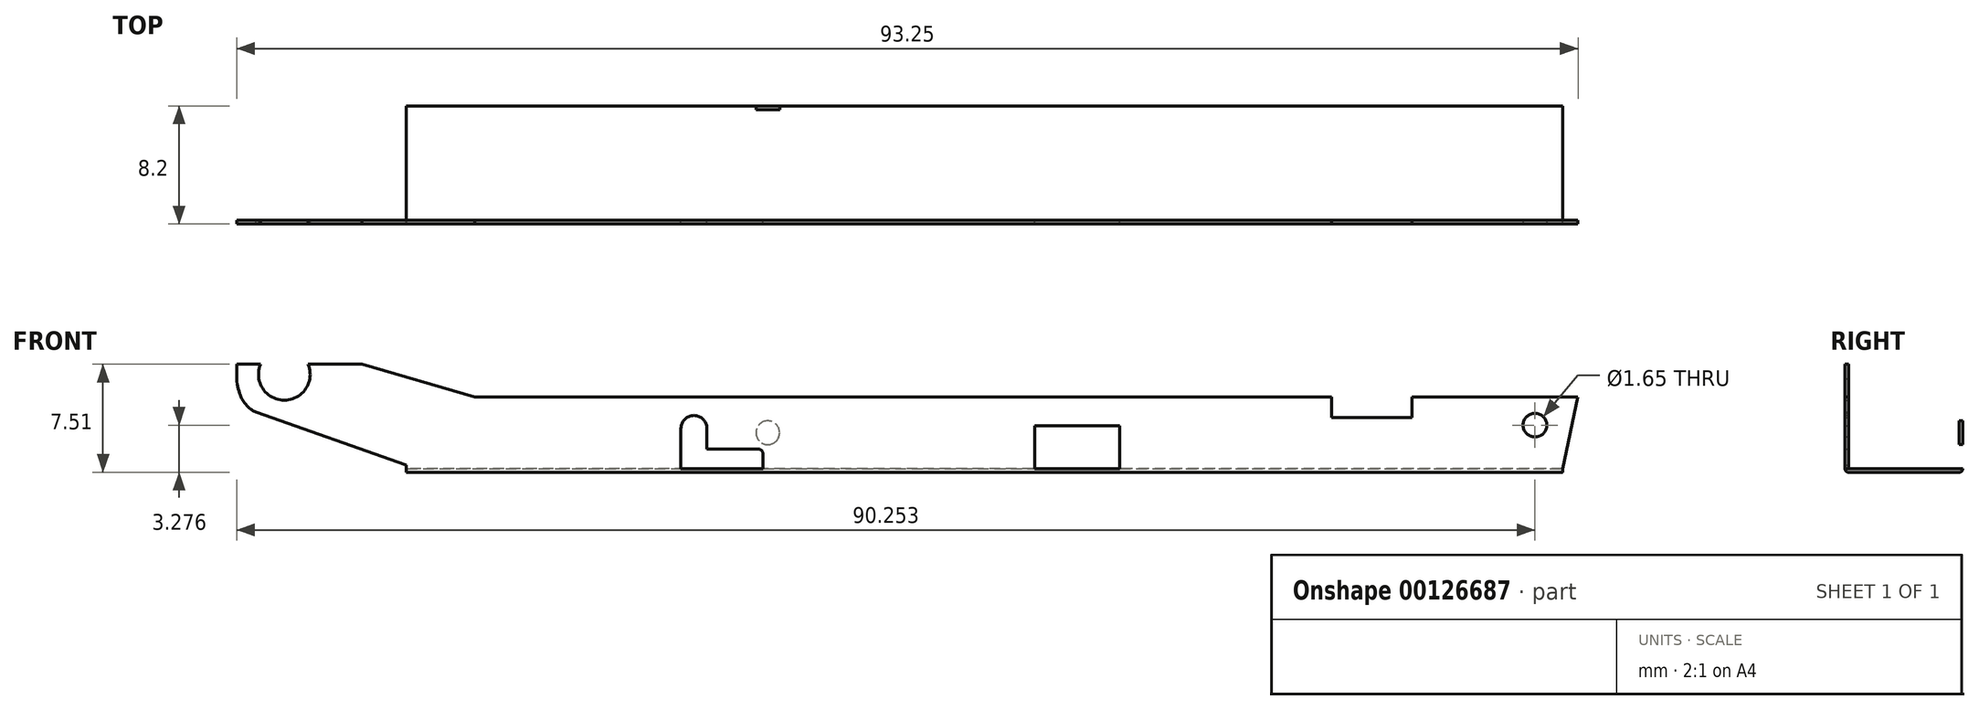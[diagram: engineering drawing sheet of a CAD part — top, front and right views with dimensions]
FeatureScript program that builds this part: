
annotation { "Feature Type Name" : "Feature", "Feature Type Description" : "" }
export const myFeature = defineFeature(function(context is Context, id is Id, definition is map)
    precondition{}
    {
        {
            var Q0;
            Q0=qCreatedBy(makeId("Front.planeOp"),FACE);
            var sketch = newSketch(context, id + "F0", { "sketchPlane" : qUnion([Q0])});
            skLineSegment(sketch, "E0", {"start": v(-40.19, 0) * mm, "end": v(40.19, 0) * mm});
            skLineSegment(sketch, "E1", {"start": v(-40.19, 0) * mm, "end": v(-40.19, 0.25) * mm});
            skLineSegment(sketch, "E2", {"start": v(-40.19, 0) * mm, "end": v(-51.99, 0) * mm, "construction": true});
            skLineSegment(sketch, "E3", {"start": v(-51.99, 0) * mm, "end": v(-51.99, 7.26) * mm});
            skLineSegment(sketch, "E4", {"start": v(-51.99, 7.26) * mm, "end": v(-50.33, 7.26) * mm});
            skPoint(sketch, "E5", {"position": v(-50.33, 7.26) * mm});
            skPoint(sketch, "E6", {"position": v(-47.03, 7.26) * mm});
            skArc(sketch, "E7", {"start": v(-50.33, 7.26) * mm, "mid": v(-48.67, 4.76) * mm, "end": v(-47.03, 7.26) * mm});
            skPoint(sketch, "E8", {"position": v(-48.68, 4.76) * mm});
            skLineSegment(sketch, "E9", {"start": v(-43.27, 7.26) * mm, "end": v(-43.27, 5) * mm, "construction": true});
            skLineSegment(sketch, "E10", {"start": v(-43.27, 5) * mm, "end": v(-35.45, 5) * mm, "construction": true});
            skLineSegment(sketch, "E11", {"start": v(-43.27, 7.26) * mm, "end": v(-35.45, 5) * mm});
            skLineSegment(sketch, "E12", {"start": v(-35.45, 5) * mm, "end": v(24.12, 5) * mm});
            skLineSegment(sketch, "E13", {"start": v(41.26, 5) * mm, "end": v(40.19, 0) * mm});
            skLineSegment(sketch, "E14", {"start": v(-40.18, 0.25) * mm, "end": v(-50.66, 3.94) * mm});
            skFitSpline(sketch, "E15", {"points": [v(-51.99, 7.26) * mm, v(-50.66, 3.94) * mm], "startDerivative": vector(-0.48, -6.82) * mm, "endDerivative": vector(1.78, -0.73) * mm});
            skLineSegment(sketch, "E16", {"start": v(-52.15, 4.99) * mm, "end": v(-51.99, 4.99) * mm});
            skLineSegment(sketch, "E17", {"start": v(-51.25, 4.18) * mm, "end": v(-51.99, 4.18) * mm});
            skLineSegment(sketch, "E18", {"start": v(-51.25, 4.18) * mm, "end": v(-50.66, 3.94) * mm});
            skPoint(sketch, "E19", {"position": v(29.7, 5) * mm});
            skPoint(sketch, "E20", {"position": v(24.12, 5) * mm});
            skLineSegment(sketch, "E21", {"start": v(29.7, 5) * mm, "end": v(29.7, 3.55) * mm});
            skLineSegment(sketch, "E22", {"start": v(24.12, 5) * mm, "end": v(24.12, 3.55) * mm});
            skLineSegment(sketch, "E23", {"start": v(24.12, 3.55) * mm, "end": v(29.7, 3.55) * mm});
            skLineSegment(sketch, "E24.trimOffspring", {"start": v(29.7, 5) * mm, "end": v(41.26, 5) * mm});
            skLineSegment(sketch, "E25.trimOffspring", {"start": v(-47.03, 7.26) * mm, "end": v(-43.27, 7.26) * mm});
            skLineSegment(sketch, "E26", {"start": v(-40.19, 0) * mm, "end": v(3.5, 0) * mm});
            skPoint(sketch, "E27", {"position": v(9.4, 0) * mm});
            skLineSegment(sketch, "E28", {"start": v(3.5, 0) * mm, "end": v(3.5, 2.98) * mm});
            skLineSegment(sketch, "E29", {"start": v(3.5, 2.98) * mm, "end": v(9.4, 2.98) * mm});
            skLineSegment(sketch, "E30", {"start": v(9.4, 2.98) * mm, "end": v(9.4, 0) * mm});
            skPoint(sketch, "E31", {"position": v(-21.1, 0) * mm});
            skPoint(sketch, "E32", {"position": v(-15.4, 0) * mm});
            skLineSegment(sketch, "E33", {"start": v(-21.1, 0) * mm, "end": v(-21.1, 2.8) * mm});
            skLineSegment(sketch, "E34", {"start": v(-15.4, 0) * mm, "end": v(-15.4, 1.04) * mm});
            skLineSegment(sketch, "E35", {"start": v(-15.73, 1.37) * mm, "end": v(-19.3, 1.37) * mm});
            skLineSegment(sketch, "E36", {"start": v(-19.3, 1.37) * mm, "end": v(-19.3, 2.8) * mm});
            skArc(sketch, "E37", {"start": v(-19.3, 2.8) * mm, "mid": v(-20.2, 3.7) * mm, "end": v(-21.1, 2.8) * mm});
            skPoint(sketch, "E38.visualSharp", {"position": v(-15.4, 1.37) * mm});
            skArc(sketch, "E38.filletArc", {"start": v(-15.4, 1.04) * mm, "mid": v(-15.5, 1.27) * mm, "end": v(-15.73, 1.37) * mm});
            skSolve(sketch);
        }
        {
            var Q0;
            Q0=qCreatedBy(makeId("Front.planeOp"),FACE);
            cPlane(context, id + "F1", {"entities" : qUnion([Q0]), "cplaneType" : CPlaneType.OFFSET, "offset" : 7.7 * mm, "oppositeDirection" : true, "width" : 150 * mm, "height" : 150 * mm});
        }
        {
            var Q0;
            Q0=qCreatedBy(id+"F1.planeOp",FACE);
            var sketch = newSketch(context, id + "F2", { "sketchPlane" : qUnion([Q0])});
            skLineSegment(sketch, "E39.0.0", {"start": v(9.4, 2.98) * mm, "end": v(9.4, 0) * mm});
            skLineSegment(sketch, "E39.0.1", {"start": v(9.4, 0) * mm, "end": v(40.19, 0) * mm});
            skLineSegment(sketch, "E39.0.2", {"start": v(40.19, 0) * mm, "end": v(41.26, 5) * mm});
            skLineSegment(sketch, "E39.0.3", {"start": v(41.26, 5) * mm, "end": v(29.7, 5) * mm});
            skLineSegment(sketch, "E39.0.4", {"start": v(29.7, 5) * mm, "end": v(29.7, 3.55) * mm});
            skLineSegment(sketch, "E39.0.5", {"start": v(29.7, 3.55) * mm, "end": v(24.12, 3.55) * mm});
            skLineSegment(sketch, "E39.0.6", {"start": v(24.12, 3.55) * mm, "end": v(24.12, 5) * mm});
            skLineSegment(sketch, "E39.0.7", {"start": v(24.12, 5) * mm, "end": v(-35.45, 5) * mm});
            skLineSegment(sketch, "E39.0.8", {"start": v(-35.45, 5) * mm, "end": v(-43.27, 7.26) * mm});
            skLineSegment(sketch, "E39.0.9", {"start": v(-43.27, 7.26) * mm, "end": v(-47.03, 7.26) * mm});
            skArc(sketch, "E39.0.10", {"start": v(-47.03, 7.26) * mm, "mid": v(-48.68, 4.76) * mm, "end": v(-50.33, 7.26) * mm});
            skLineSegment(sketch, "E39.0.11", {"start": v(-50.33, 7.26) * mm, "end": v(-51.99, 7.26) * mm});
            skLineSegment(sketch, "E39.0.12", {"start": v(-51.99, 7.26) * mm, "end": v(-51.99, 6.26) * mm});
            skFitSpline(sketch, "E39.0.13", {"points": [v(-51.99, 7.26) * mm, v(-52.15, 4.99) * mm, v(-51.25, 4.18) * mm, v(-50.66, 3.94) * mm]});
            skLineSegment(sketch, "E39.0.14", {"start": v(-50.66, 3.94) * mm, "end": v(-40.18, 0.25) * mm});
            skLineSegment(sketch, "E39.0.15", {"start": v(-40.19, 0.25) * mm, "end": v(-40.19, 0) * mm});
            skLineSegment(sketch, "E39.0.16", {"start": v(-40.19, 0) * mm, "end": v(-21.1, 0) * mm});
            skLineSegment(sketch, "E39.0.23", {"start": v(-15.4, 0) * mm, "end": v(3.5, 0) * mm});
            skLineSegment(sketch, "E39.0.24", {"start": v(3.5, 0) * mm, "end": v(3.5, 2.98) * mm});
            skLineSegment(sketch, "E39.0.25", {"start": v(3.5, 2.98) * mm, "end": v(9.4, 2.98) * mm});
            skLineSegment(sketch, "E40.0", {"start": v(-40.19, 0) * mm, "end": v(3.5, 0) * mm});
            skLineSegment(sketch, "E41.0", {"start": v(-40.19, 0) * mm, "end": v(40.19, 0) * mm});
            skSolve(sketch);
        }
        {
            var Q0;
            {var subQ5=sQuery(id+"F0.wireOp",EDGE,"E1");Q0=makeQuery(id+"F0.imprint","IMPRINT",FACE,{"disambiguationData":[TD([[makeQuery(id+"F0.imprint","IMPRINT",EDGE,{"derivedFrom":subQ5}),-1.0]])]});}
            extrude(context, id + "F3", {"entities" : qUnion([Q0]), "depth" : 0.25 * mm});
        }
        {
            var Q0;
            {var subQ4=sQuery(id+"F2.wireOp",EDGE,"E39.0.0");Q0=makeQuery(id+"F2.imprint","IMPRINT",FACE,{"disambiguationData":[TD([[makeQuery(id+"F2.imprint","IMPRINT",EDGE,{"derivedFrom":subQ4}),1.0]])]});}
            extrude(context, id + "F4", {"entities" : qUnion([Q0]), "oppositeDirection" : true, "depth" : 0.25 * mm});
        }
        {
            var Q0;
            Q0=qCreatedBy(makeId("Top.planeOp"),FACE);
            var sketch = newSketch(context, id + "F5", { "sketchPlane" : qUnion([Q0])});
            skPoint(sketch, "E42.0", {"position": v(40.19, 0) * mm});
            skPoint(sketch, "E43.0", {"position": v(40.19, 7.7) * mm});
            skPoint(sketch, "E44.0", {"position": v(-40.19, 0) * mm});
            skPoint(sketch, "E45.0", {"position": v(-40.18, 7.7) * mm});
            skLineSegment(sketch, "E46.bottom", {"start": v(40.18, 0) * mm, "end": v(-40.18, 0) * mm});
            skLineSegment(sketch, "E46.top", {"start": v(40.18, 7.7) * mm, "end": v(-40.18, 7.7) * mm});
            skLineSegment(sketch, "E46.left", {"start": v(40.19, 0) * mm, "end": v(40.19, 7.7) * mm});
            skLineSegment(sketch, "E46.right", {"start": v(-40.18, 0) * mm, "end": v(-40.18, 7.7) * mm});
            skSolve(sketch);
        }
        {
            var Q0;
            Q0=makeQuery(id+"F5.imprint","IMPRINT",FACE,{"disambiguationData":[TD([[makeQuery(id+"F5.imprint","IMPRINT",EDGE,{"derivedFrom":sQuery(id+"F5.wireOp",EDGE,"E46.bottom")}),-1.0]])]});
            extrude(context, id + "F6", {"entities" : qUnion([Q0]), "oppositeDirection" : true, "depth" : 0.25 * mm});
        }
        {
            var Q0;
            Q0=makeQuery(id+"F6.opExtrude","SWEPT_FACE",FACE,{"disambiguationData":[OSD([sQuery(id+"F5.wireOp",EDGE,"E46.right")])]});
            var sketch = newSketch(context, id + "F7", { "sketchPlane" : qUnion([Q0])});
            skPoint(sketch, "E47.0", {"position": v(0.25, 0) * mm});
            skPoint(sketch, "E48.0", {"position": v(0, -0.25) * mm});
            skArc(sketch, "E49", {"start": v(0, -0.25) * mm, "mid": v(0.18, -0.18) * mm, "end": v(0.25, 0) * mm});
            skLineSegment(sketch, "E50", {"start": v(0.25, 0) * mm, "end": v(0, 0) * mm});
            skLineSegment(sketch, "E51", {"start": v(0, 0) * mm, "end": v(0, -0.25) * mm});
            skSolve(sketch);
        }
        {
            var Q0;
            Q0=makeQuery(id+"F7.imprint","IMPRINT",FACE,{"disambiguationData":[TD([[makeQuery(id+"F7.imprint","IMPRINT",EDGE,{"derivedFrom":sQuery(id+"F7.wireOp",EDGE,"E49")}),1.0]])]});
            var Q1;
            Q1 = qConstructionFilter(qBodyType(qCreatedBy(id + "F7" ,EDGE), BodyType.WIRE), ConstructionObject.NO);
            var Q2;
            Q2=makeQuery(id+"F6.opExtrude","SWEPT_FACE",FACE,{"disambiguationData":[OSD([sQuery(id+"F5.wireOp",EDGE,"E46.left")])]});
            extrude(context, id + "F8", {"entities" : qUnion([Q0]), "operationType" : NewBodyOperationType.ADD, "surfaceEntities" : qUnion([Q1]), "endBound" : BoundingType.UP_TO_SURFACE, "oppositeDirection" : true, "endBoundEntityFace" : qUnion([Q2]), "depth" : 1.77 * mm});
        }
        {
            var Q0;
            Q0=makeQuery(id+"F6.opExtrude","SWEPT_FACE",FACE,{"disambiguationData":[OSD([sQuery(id+"F5.wireOp",EDGE,"E46.right")])]});
            var sketch = newSketch(context, id + "F9", { "sketchPlane" : qUnion([Q0])});
            skPoint(sketch, "E52.0", {"position": v(-7.95, 0) * mm});
            skArc(sketch, "E53", {"start": v(-7.95, 0) * mm, "mid": v(-7.88, -0.18) * mm, "end": v(-7.7, -0.25) * mm});
            skLineSegment(sketch, "E54", {"start": v(-7.7, 0) * mm, "end": v(-7.95, 0) * mm});
            skLineSegment(sketch, "E55", {"start": v(-7.7, 0) * mm, "end": v(-7.7, -0.25) * mm});
            skSolve(sketch);
        }
        {
            var Q0;
            Q0=makeQuery(id+"F9.imprint","IMPRINT",FACE,{"disambiguationData":[TD([[makeQuery(id+"F9.imprint","IMPRINT",EDGE,{"derivedFrom":sQuery(id+"F9.wireOp",EDGE,"E53")}),1.0]])]});
            var Q1;
            Q1=makeQuery(id+"F6.opExtrude","SWEPT_FACE",FACE,{"disambiguationData":[OSD([sQuery(id+"F5.wireOp",EDGE,"E46.left")])]});
            extrude(context, id + "F10", {"entities" : qUnion([Q0]), "operationType" : NewBodyOperationType.ADD, "endBound" : BoundingType.UP_TO_SURFACE, "oppositeDirection" : true, "endBoundEntityFace" : qUnion([Q1]), "depth" : 25 * mm});
        }
        {
            var Q0;
            Q0=makeQuery(id+"F3.opExtrude","CAP_FACE",FACE,{"disambiguationData":[OSD([sQuery(id+"F0.wireOp",EDGE,"E0"),sQuery(id+"F0.wireOp",EDGE,"E1"),sQuery(id+"F0.wireOp",EDGE,"E3"),sQuery(id+"F0.wireOp",EDGE,"E4"),sQuery(id+"F0.wireOp",EDGE,"E7"),sQuery(id+"F0.wireOp",EDGE,"E11"),sQuery(id+"F0.wireOp",EDGE,"E12"),sQuery(id+"F0.wireOp",EDGE,"E13"),sQuery(id+"F0.wireOp",EDGE,"E14"),sQuery(id+"F0.wireOp",EDGE,"E15"),sQuery(id+"F0.wireOp",EDGE,"E21"),sQuery(id+"F0.wireOp",EDGE,"E22"),sQuery(id+"F0.wireOp",EDGE,"E23"),sQuery(id+"F0.wireOp",EDGE,"E24.trimOffspring"),sQuery(id+"F0.wireOp",EDGE,"E25.trimOffspring"),sQuery(id+"F0.wireOp",EDGE,"E26"),sQuery(id+"F0.wireOp",EDGE,"E28"),sQuery(id+"F0.wireOp",EDGE,"E29"),sQuery(id+"F0.wireOp",EDGE,"E30"),sQuery(id+"F0.wireOp",EDGE,"E33"),sQuery(id+"F0.wireOp",EDGE,"E34"),sQuery(id+"F0.wireOp",EDGE,"E35"),sQuery(id+"F0.wireOp",EDGE,"E36"),sQuery(id+"F0.wireOp",EDGE,"E37"),sQuery(id+"F0.wireOp",EDGE,"E38.filletArc")])],"isStart":false});
            var sketch = newSketch(context, id + "F11", { "sketchPlane" : qUnion([Q0])});
            skCircle(sketch, "E56", {"center": v(38.26, 3.03) * mm, "radius": 0.82 * mm});
            skLineSegment(sketch, "E57", {"start": v(38.26, 5) * mm, "end": v(38.26, 0) * mm});
            skCircle(sketch, "E58", {"center": v(-15.07, 2.5) * mm, "radius": 0.82 * mm});
            skLineSegment(sketch, "E59", {"start": v(-15.07, 5) * mm, "end": v(-15.07, 0) * mm});
            skSolve(sketch);
        }
        {
            var Q0;
            {var subQ0=sQuery(id+"F11.wireOp",EDGE,"E57");var subQ1=sQuery(id+"F11.wireOp",EDGE,"E56");var subQ2=makeQuery(id+"F11.imprint","INTERSECT",VERTEX,{"disambiguationData":[OD(0.0)],"derivedFrom":[subQ1,subQ0]});Q0=makeQuery(id+"F11.imprint","IMPRINT",FACE,{"disambiguationData":[TD([[makeQuery(id+"F11.imprint","IMPRINT",EDGE,{"disambiguationData":[TD([[subQ2,1.0]])],"derivedFrom":subQ1}),1.0]])]});}
            var Q1;
            {var subQ0=sQuery(id+"F11.wireOp",EDGE,"E57");var subQ1=sQuery(id+"F11.wireOp",EDGE,"E56");var subQ2=makeQuery(id+"F11.imprint","INTERSECT",VERTEX,{"disambiguationData":[OD(0.0)],"derivedFrom":[subQ1,subQ0]});Q1=makeQuery(id+"F11.imprint","IMPRINT",FACE,{"disambiguationData":[TD([[makeQuery(id+"F11.imprint","IMPRINT",EDGE,{"disambiguationData":[TD([[subQ2,-1.0]])],"derivedFrom":subQ1}),1.0]])]});}
            extrude(context, id + "F12", {"entities" : qUnion([Q0, Q1]), "operationType" : NewBodyOperationType.REMOVE, "endBound" : BoundingType.THROUGH_ALL, "oppositeDirection" : true, "depth" : 25 * mm});
        }
        {
            var Q0;
            Q0=makeQuery(id+"F4.opExtrude","CAP_FACE",FACE,{"disambiguationData":[OSD([sQuery(id+"F2.wireOp",EDGE,"E39.0.0"),sQuery(id+"F2.wireOp",EDGE,"E39.0.2"),sQuery(id+"F2.wireOp",EDGE,"E39.0.3"),sQuery(id+"F2.wireOp",EDGE,"E39.0.4"),sQuery(id+"F2.wireOp",EDGE,"E39.0.5"),sQuery(id+"F2.wireOp",EDGE,"E39.0.6"),sQuery(id+"F2.wireOp",EDGE,"E39.0.7"),sQuery(id+"F2.wireOp",EDGE,"E39.0.8"),sQuery(id+"F2.wireOp",EDGE,"E39.0.9"),sQuery(id+"F2.wireOp",EDGE,"E39.0.10"),sQuery(id+"F2.wireOp",EDGE,"E39.0.11"),sQuery(id+"F2.wireOp",EDGE,"E39.0.12"),sQuery(id+"F2.wireOp",EDGE,"E39.0.13"),sQuery(id+"F2.wireOp",EDGE,"E39.0.14"),sQuery(id+"F2.wireOp",EDGE,"E39.0.15"),sQuery(id+"F2.wireOp",EDGE,"E39.0.24"),sQuery(id+"F2.wireOp",EDGE,"E39.0.25"),sQuery(id+"F2.wireOp",EDGE,"E41.0")])],"isStart":false});
            var sketch = newSketch(context, id + "F13", { "sketchPlane" : qUnion([Q0])});
            skCircle(sketch, "E60.0", {"center": v(15.07, 2.5) * mm, "radius": 0.82 * mm});
            skSolve(sketch);
        }
        {
            var Q0;
            Q0=makeQuery(id+"F13.imprint","IMPRINT",FACE,{"disambiguationData":[TD([[makeQuery(id+"F13.imprint","IMPRINT",EDGE,{"derivedFrom":sQuery(id+"F13.wireOp",EDGE,"E60.0")}),-1.0]])]});
            extrude(context, id + "F14", {"entities" : qUnion([Q0]), "operationType" : NewBodyOperationType.REMOVE, "oppositeDirection" : true, "depth" : 2 * mm});
        }
    });
